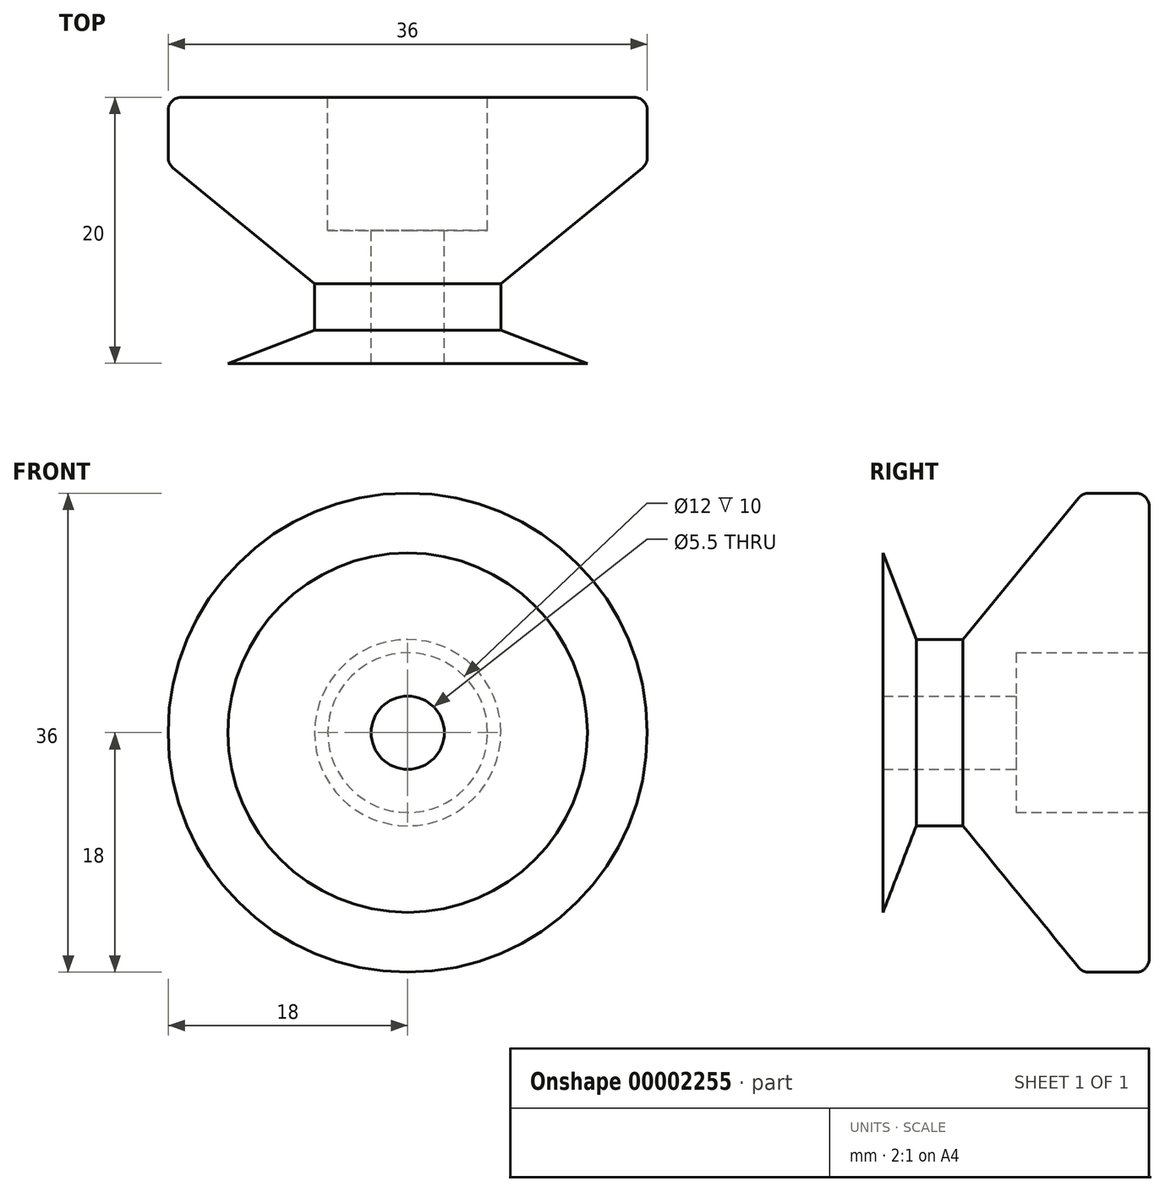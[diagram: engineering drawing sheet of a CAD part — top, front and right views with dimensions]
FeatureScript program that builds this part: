
annotation { "Feature Type Name" : "Feature", "Feature Type Description" : "" }
export const myFeature = defineFeature(function(context is Context, id is Id, definition is map)
    precondition{}
    {
        {
            var Q0;
            Q0=qCreatedBy(makeId("Right.planeOp"),FACE);
            var sketch = newSketch(context, id + "F0", { "sketchPlane" : qUnion([Q0])});
            skLineSegment(sketch, "E0", {"start": v(26.93, 664.55) * mm, "end": v(27.09, 628.55) * mm});
            skLineSegment(sketch, "E1.bottom", {"start": v(-54.74, 0) * mm, "end": v(-34.74, 0) * mm});
            skLineSegment(sketch, "E1.right", {"start": v(-34.74, 0) * mm, "end": v(-34.74, 18) * mm});
            skLineSegment(sketch, "E2", {"start": v(-54.74, 0) * mm, "end": v(-54.74, 13.5) * mm});
            skLineSegment(sketch, "E3", {"start": v(-34.74, 18) * mm, "end": v(-39.74, 18) * mm});
            skLineSegment(sketch, "E4", {"start": v(-39.74, 18) * mm, "end": v(-48.74, 7) * mm});
            skLineSegment(sketch, "E5", {"start": v(-48.74, 7) * mm, "end": v(-52.24, 7) * mm});
            skLineSegment(sketch, "E6", {"start": v(-52.24, 7) * mm, "end": v(-54.74, 13.5) * mm});
            skSolve(sketch);
        }
        {
            var Q0;
            Q0 = qSketchRegion(id + "F0", true);
            var Q1;
            Q1=sQuery(id+"F0.wireOp",EDGE,"E1.bottom");
            revolve(context, id + "F1", {"entities" : qUnion([Q0]), "axis" : qUnion([Q1]), "revolveType" : RevolveType.FULL});
        }
        {
            var Q0;
            Q0=makeQuery(id+"F1.opRevolve","SWEPT_EDGE",EDGE,{"disambiguationData":[OSD([sQuery(id+"F0.wireOp",EDGE,"E1.right"),sQuery(id+"F0.wireOp",EDGE,"E3")])]});
            fillet(context, id + "F2", {"entities" : qUnion([Q0]), "radius" : 1 * mm, "tangentPropagation" : true, "allowEdgeOverflow" : false});
        }
        {
            var Q0;
            Q0=makeQuery(id+"F1.opRevolve","SWEPT_EDGE",EDGE,{"disambiguationData":[OSD([sQuery(id+"F0.wireOp",EDGE,"E3"),sQuery(id+"F0.wireOp",EDGE,"E4")])]});
            fillet(context, id + "F3", {"entities" : qUnion([Q0]), "radius" : 1 * mm, "tangentPropagation" : true, "allowEdgeOverflow" : false});
        }
        {
            var Q0;
            Q0=makeQuery(id+"F1.opRevolve","SWEPT_FACE",FACE,{"disambiguationData":[OSD([sQuery(id+"F0.wireOp",EDGE,"E1.right")])]});
            var sketch = newSketch(context, id + "F4", { "sketchPlane" : qUnion([Q0])});
            skCircle(sketch, "E7", {"center": v(0, 0) * mm, "radius": 6 * mm});
            skCircle(sketch, "E8", {"center": v(0, 0) * mm, "radius": 2.75 * mm});
            skSolve(sketch);
        }
        {
            var Q0;
            Q0 = qSketchRegion(id + "F4", true);
            extrude(context, id + "F5", {"entities" : qUnion([Q0]), "operationType" : NewBodyOperationType.REMOVE, "oppositeDirection" : true, "depth" : 10 * mm});
        }
        {
            var Q0;
            Q0=makeQuery(id+"F5.boolean.opBoolean","SPLIT",FACE,{"disambiguationData":[TD([makeQuery(id+"F5.opExtrude","SWEPT_FACE",FACE,{"disambiguationData":[OSD([sQuery(id+"F4.wireOp",EDGE,"E8")])]})])],"derivedFrom":makeQuery(id+"F1.opRevolve","SWEPT_FACE",FACE,{"disambiguationData":[OSD([sQuery(id+"F0.wireOp",EDGE,"E1.right")])]})});
            extrude(context, id + "F6", {"entities" : qUnion([Q0]), "operationType" : NewBodyOperationType.REMOVE, "oppositeDirection" : true, "depth" : 43.3 * mm});
        }
    });
